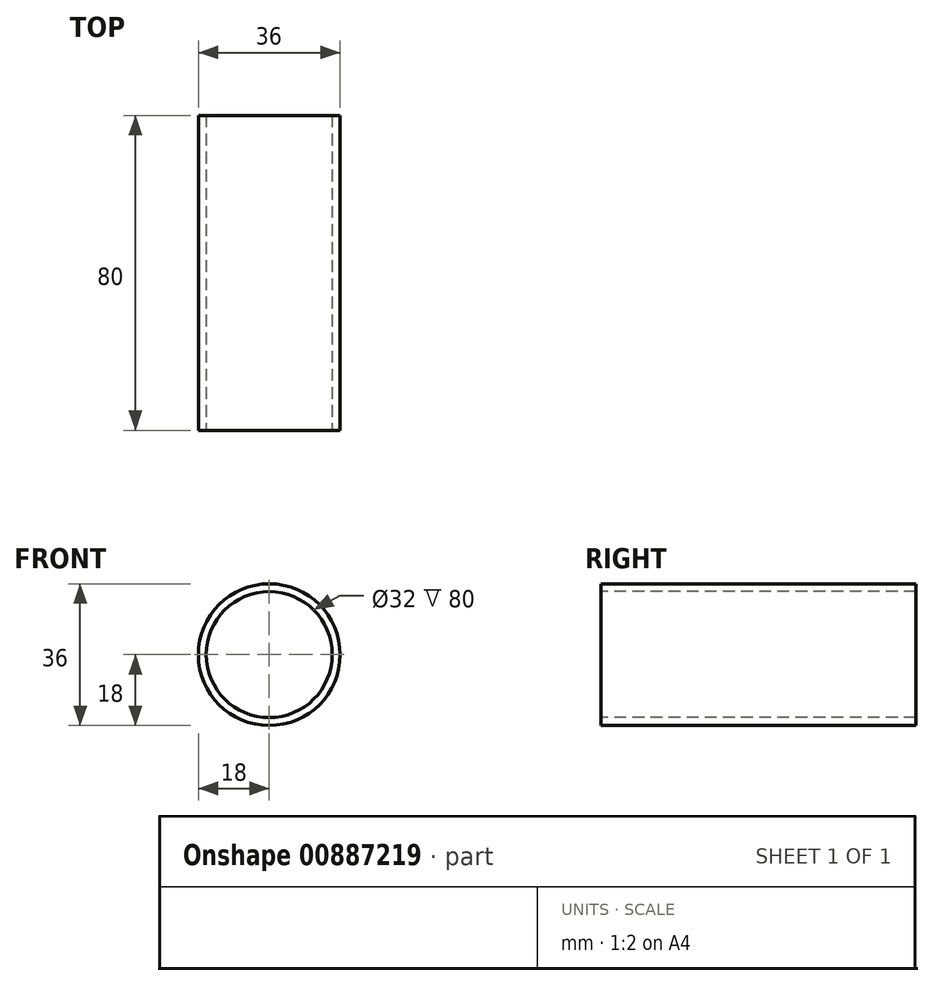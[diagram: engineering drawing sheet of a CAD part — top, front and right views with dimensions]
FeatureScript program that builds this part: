
annotation { "Feature Type Name" : "Feature", "Feature Type Description" : "" }
export const myFeature = defineFeature(function(context is Context, id is Id, definition is map)
    precondition{}
    {
        {
            var Q0;
            Q0=qCreatedBy(makeId("Front.planeOp"),FACE);
            var sketch = newSketch(context, id + "F0", { "sketchPlane" : qUnion([Q0])});
            skCircle(sketch, "E0", {"center": v(0, 0) * mm, "radius": 18 * mm});
            skCircle(sketch, "E1", {"center": v(0, 0) * mm, "radius": 16 * mm});
            skSolve(sketch);
        }
        {
            var Q0;
            Q0 = qSketchRegion(id + "F0", true);
            extrude(context, id + "F1", {"entities" : qUnion([Q0]), "endBound" : BoundingType.SYMMETRIC, "oppositeDirection" : true, "depth" : 80 * mm, "offsetDistance" : 25 * mm});
        }
    });
